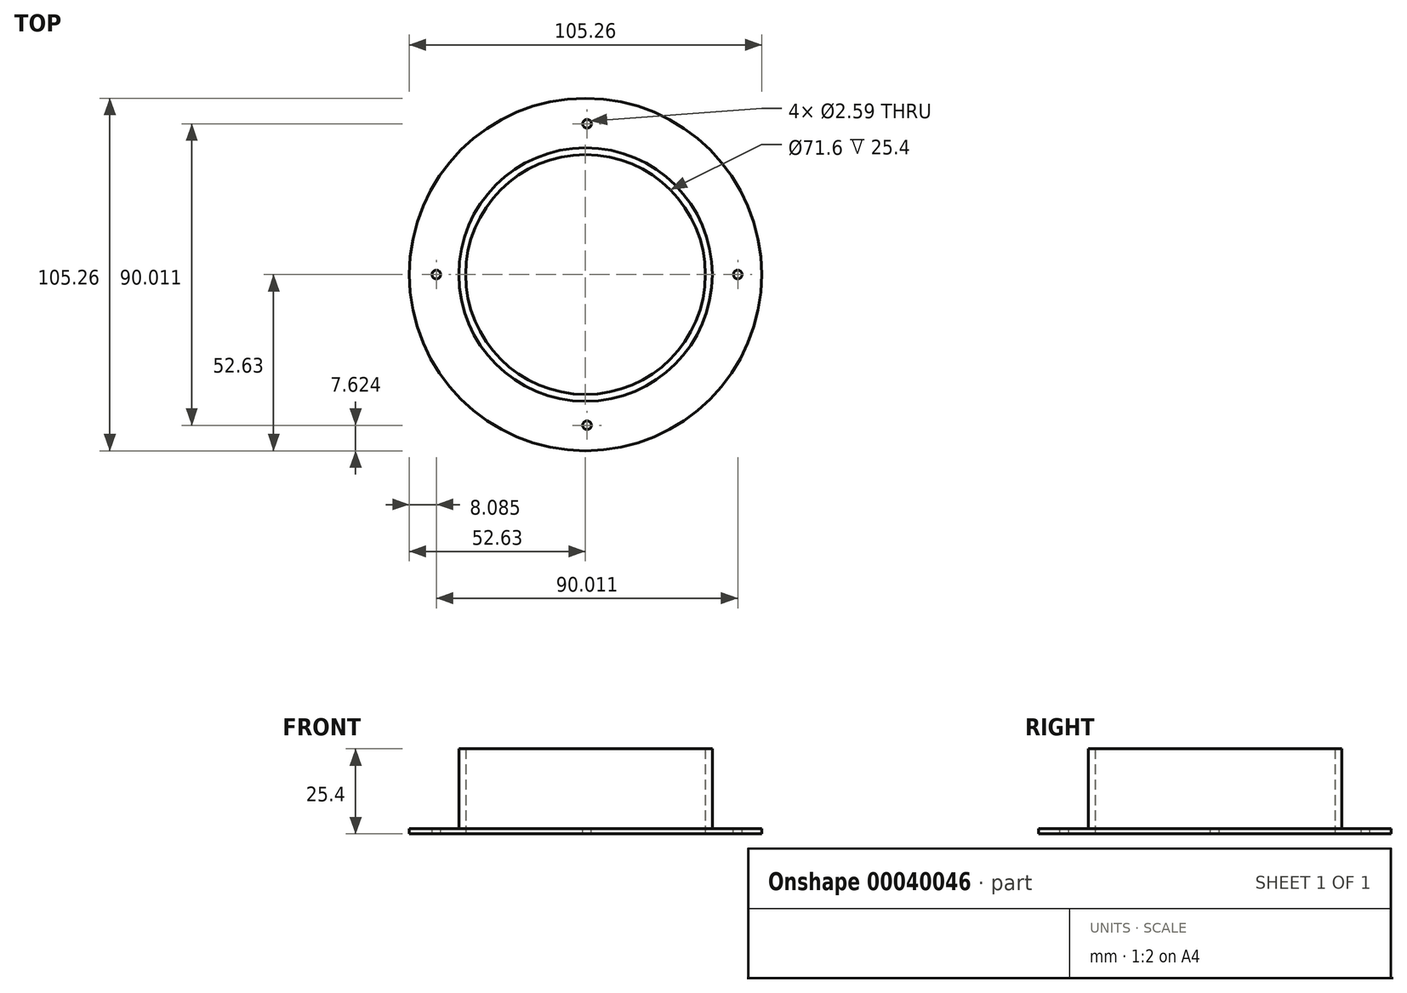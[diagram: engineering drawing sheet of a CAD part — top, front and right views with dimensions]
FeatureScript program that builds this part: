
annotation { "Feature Type Name" : "Feature", "Feature Type Description" : "" }
export const myFeature = defineFeature(function(context is Context, id is Id, definition is map)
    precondition{}
    {
        {
            var Q0;
            Q0=qCreatedBy(makeId("Top.planeOp"),FACE);
            var sketch = newSketch(context, id + "F0", { "sketchPlane" : qUnion([Q0])});
            skCircle(sketch, "E0", {"center": v(0, 0) * mm, "radius": 37.85 * mm});
            skSolve(sketch);
        }
        {
            var Q0;
            Q0=makeQuery(id+"F0.imprint","IMPRINT",FACE,{"disambiguationData":[TD([[makeQuery(id+"F0.imprint","IMPRINT",EDGE,{"derivedFrom":sQuery(id+"F0.wireOp",EDGE,"E0")}),1.0]])]});
            extrude(context, id + "F1", {"entities" : qUnion([Q0]), "depth" : 25.4 * mm});
        }
        {
            var Q0;
            Q0=qCreatedBy(makeId("Top.planeOp"),FACE);
            var sketch = newSketch(context, id + "F2", { "sketchPlane" : qUnion([Q0])});
            skCircle(sketch, "E1", {"center": v(0, 0) * mm, "radius": 52.63 * mm});
            skSolve(sketch);
        }
        {
            var Q0;
            Q0=makeQuery(id+"F2.imprint","IMPRINT",FACE,{"disambiguationData":[TD([[makeQuery(id+"F2.imprint","IMPRINT",EDGE,{"derivedFrom":sQuery(id+"F2.wireOp",EDGE,"E1")}),1.0]])]});
            extrude(context, id + "F3", {"entities" : qUnion([Q0]), "operationType" : NewBodyOperationType.ADD, "depth" : 1.59 * mm});
        }
        {
            var Q0;
            Q0=qCreatedBy(makeId("Top.planeOp"),FACE);
            var sketch = newSketch(context, id + "F4", { "sketchPlane" : qUnion([Q0])});
            skCircle(sketch, "E2", {"center": v(0, 0) * mm, "radius": 35.8 * mm});
            skSolve(sketch);
        }
        {
            var Q0;
            Q0 = qSketchRegion(id + "F4", true);
            extrude(context, id + "F5", {"entities" : qUnion([Q0]), "operationType" : NewBodyOperationType.REMOVE, "endBound" : BoundingType.UP_TO_NEXT, "depth" : 25.4 * mm});
        }
        {
            var Q0;
            Q0=makeQuery(id+"F3.opExtrude","CAP_FACE",FACE,{"disambiguationData":[OSD([sQuery(id+"F2.wireOp",EDGE,"E1")])],"isStart":false});
            var sketch = newSketch(context, id + "F6", { "sketchPlane" : qUnion([Q0])});
            skCircle(sketch, "E3", {"center": v(45.47, 0) * mm, "radius": 1.3 * mm});
            skCircle(sketch, "E4.1.0", {"center": v(0.46, -45) * mm, "radius": 1.3 * mm});
            skCircle(sketch, "E4.2.0", {"center": v(-44.55, 0) * mm, "radius": 1.3 * mm});
            skCircle(sketch, "E4.3.0", {"center": v(0.46, 45) * mm, "radius": 1.3 * mm});
            skPoint(sketch, "E4.center", {"position": v(0.46, 0) * mm});
            skLineSegment(sketch, "E4.anchor1", {"start": v(0.46, 0) * mm, "end": v(45.47, 0) * mm, "construction": true});
            skLineSegment(sketch, "E4.anchor2", {"start": v(0.46, 0) * mm, "end": v(0.46, 45) * mm, "construction": true});
            skSolve(sketch);
        }
        {
            var Q0;
            Q0 = qSketchRegion(id + "F6", true);
            extrude(context, id + "F7", {"entities" : qUnion([Q0]), "operationType" : NewBodyOperationType.REMOVE, "endBound" : BoundingType.THROUGH_ALL, "oppositeDirection" : true, "depth" : 25.4 * mm});
        }
    });
